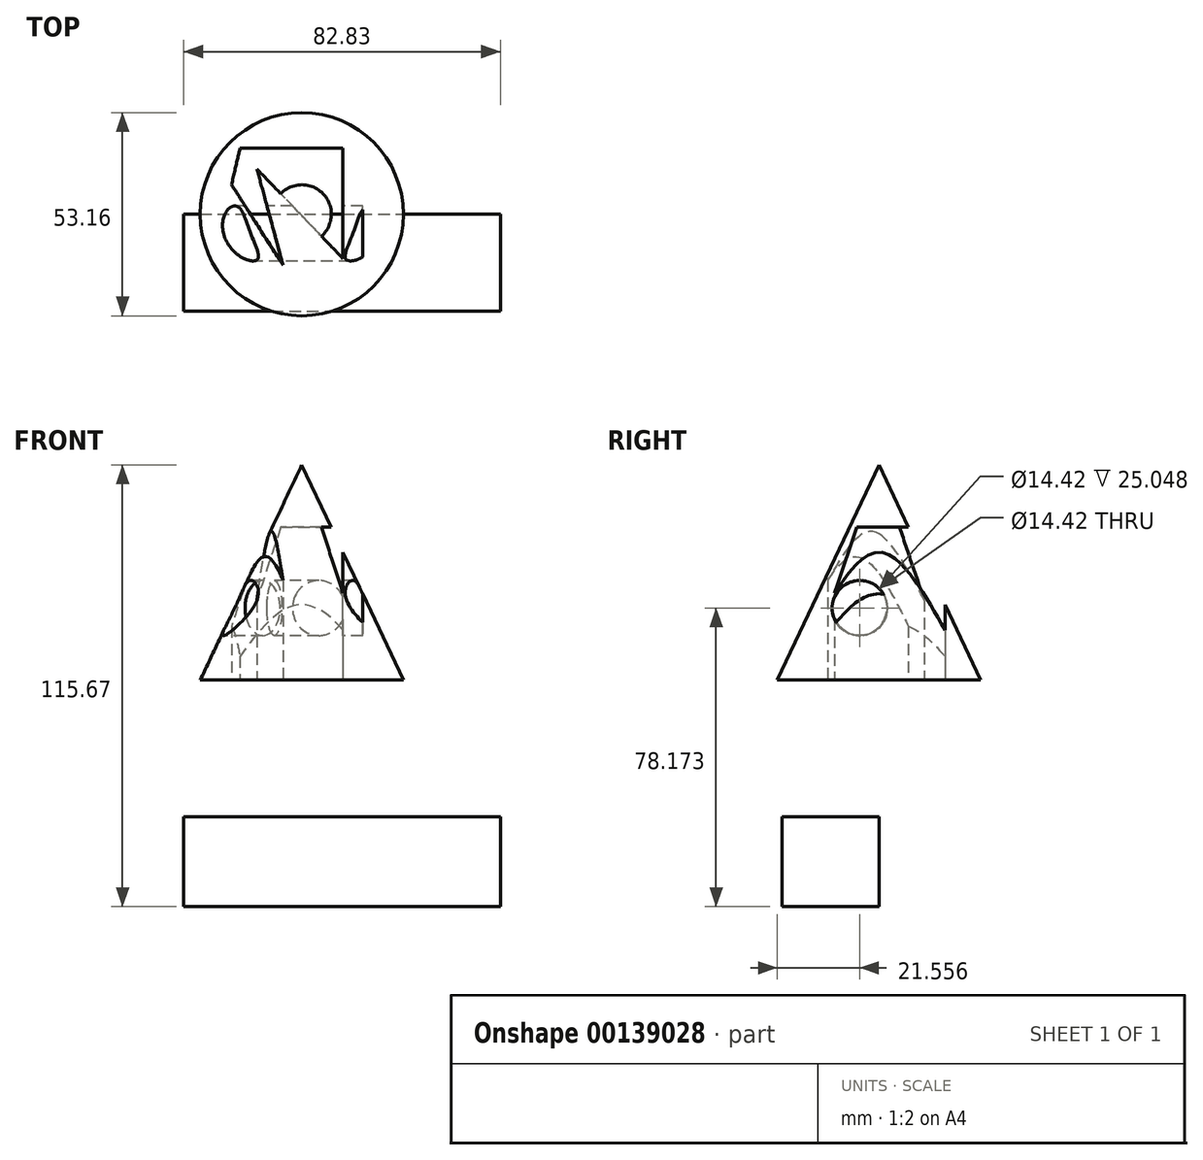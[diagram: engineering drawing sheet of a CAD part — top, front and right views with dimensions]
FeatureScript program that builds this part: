
annotation { "Feature Type Name" : "Feature", "Feature Type Description" : "" }
export const myFeature = defineFeature(function(context is Context, id is Id, definition is map)
    precondition{}
    {
        {
            var Q0;
            Q0=qCreatedBy(makeId("Front.planeOp"),FACE);
            var sketch = newSketch(context, id + "F0", { "sketchPlane" : qUnion([Q0])});
            skLineSegment(sketch, "E0", {"start": v(8.2, 62.37) * mm, "end": v(8.2, 6) * mm});
            skLineSegment(sketch, "E1", {"start": v(-18.37, 6) * mm, "end": v(8.2, 6) * mm});
            skLineSegment(sketch, "E2", {"start": v(-18.37, 6) * mm, "end": v(8.2, 62.37) * mm});
            skSolve(sketch);
        }
        {
            var Q0;
            Q0=makeQuery(id+"F0.imprint","IMPRINT",FACE,{"disambiguationData":[TD([[makeQuery(id+"F0.imprint","IMPRINT",EDGE,{"derivedFrom":sQuery(id+"F0.wireOp",EDGE,"E0")}),-1.0]])]});
            var Q1;
            Q1=sQuery(id+"F0.wireOp",EDGE,"E0");
            revolve(context, id + "F1", {"entities" : qUnion([Q0]), "axis" : qUnion([Q1]), "revolveType" : RevolveType.FULL});
        }
        {
            var Q0;
            Q0=qCreatedBy(makeId("Front.planeOp"),FACE);
            var sketch = newSketch(context, id + "F2", { "sketchPlane" : qUnion([Q0])});
            skLineSegment(sketch, "E3.bottom", {"start": v(-22.67, -53.3) * mm, "end": v(60.16, -53.3) * mm});
            skLineSegment(sketch, "E3.top", {"start": v(-22.67, -29.77) * mm, "end": v(60.16, -29.77) * mm});
            skLineSegment(sketch, "E3.left", {"start": v(-22.67, -53.3) * mm, "end": v(-22.67, -29.77) * mm});
            skLineSegment(sketch, "E3.right", {"start": v(60.16, -53.3) * mm, "end": v(60.16, -29.77) * mm});
            skSolve(sketch);
        }
        {
            var Q0;
            Q0 = qSketchRegion(id + "F2", true);
            extrude(context, id + "F3", {"entities" : qUnion([Q0]), "depth" : 25.4 * mm});
        }
        {
            var Q0;
            Q0=qCreatedBy(makeId("Right.planeOp"),FACE);
            var sketch = newSketch(context, id + "F4", { "sketchPlane" : qUnion([Q0])});
            skCircle(sketch, "E4", {"center": v(-5.02, 24.87) * mm, "radius": 7.21 * mm});
            skSolve(sketch);
        }
        {
            var Q0;
            Q0 = qSketchRegion(id + "F4", true);
            extrude(context, id + "F5", {"entities" : qUnion([Q0]), "operationType" : NewBodyOperationType.REMOVE, "endBound" : BoundingType.SYMMETRIC, "depth" : 48.26 * mm});
        }
        {
            var Q0;
            Q0=makeQuery(id+"F1.opRevolve","SWEPT_FACE",FACE,{"disambiguationData":[OSD([sQuery(id+"F0.wireOp",EDGE,"E1")])]});
            var sketch = newSketch(context, id + "F6", { "sketchPlane" : qUnion([Q0])});
            skLineSegment(sketch, "E5", {"start": v(0, -17.28) * mm, "end": v(19, -17.28) * mm});
            skLineSegment(sketch, "E6", {"start": v(19, -17.52) * mm, "end": v(19, 11.89) * mm});
            skLineSegment(sketch, "E7", {"start": v(19.24, 11.89) * mm, "end": v(-3.55, -11.89) * mm});
            skLineSegment(sketch, "E8", {"start": v(-3.55, -11.89) * mm, "end": v(3.3, 13.36) * mm});
            skLineSegment(sketch, "E9", {"start": v(3.3, 13.36) * mm, "end": v(-10.17, -7.72) * mm});
            skLineSegment(sketch, "E10", {"start": v(-10.17, -7.72) * mm, "end": v(-7.96, -17.28) * mm});
            skLineSegment(sketch, "E11", {"start": v(0, -17.28) * mm, "end": v(-7.96, -17.28) * mm});
            skSolve(sketch);
        }
        {
            var Q0;
            Q0 = qSketchRegion(id + "F6", true);
            extrude(context, id + "F7", {"entities" : qUnion([Q0]), "operationType" : NewBodyOperationType.REMOVE, "oppositeDirection" : true, "depth" : 40 * mm});
        }
    });
